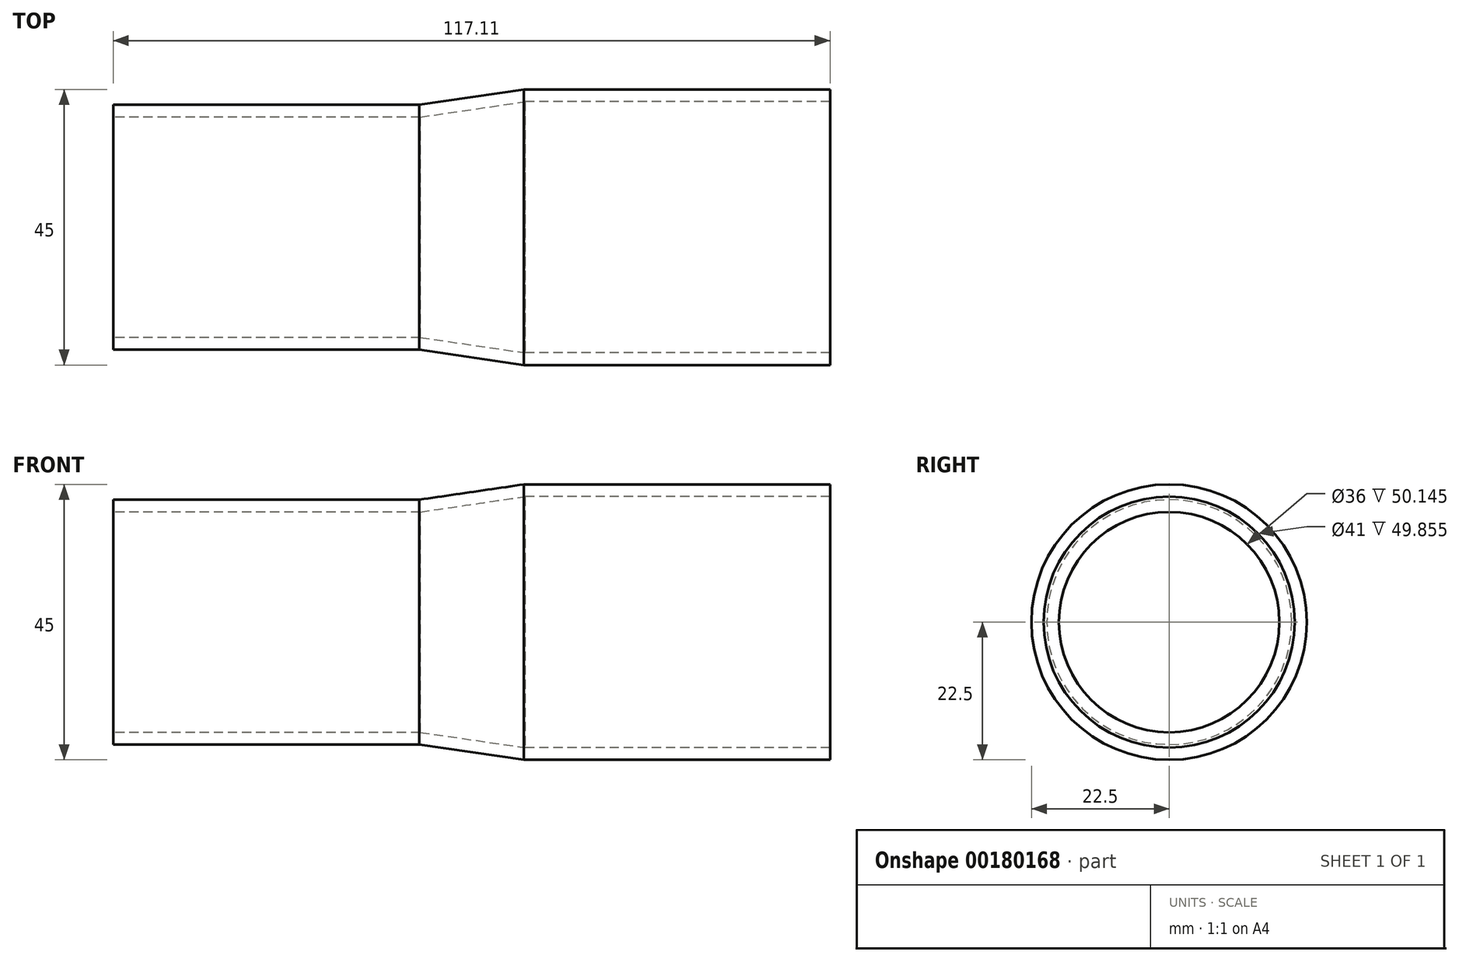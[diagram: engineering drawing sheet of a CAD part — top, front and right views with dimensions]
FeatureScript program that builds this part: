
annotation { "Feature Type Name" : "Feature", "Feature Type Description" : "" }
export const myFeature = defineFeature(function(context is Context, id is Id, definition is map)
    precondition{}
    {
        {
            var Q0;
            Q0=qCreatedBy(makeId("Front.planeOp"),FACE);
            var sketch = newSketch(context, id + "F0", { "sketchPlane" : qUnion([Q0])});
            skLineSegment(sketch, "E0", {"start": v(-49.34, 22.58) * mm, "end": v(0.66, 22.58) * mm});
            skLineSegment(sketch, "E1", {"start": v(0.66, 22.58) * mm, "end": v(17.77, 25.08) * mm});
            skLineSegment(sketch, "E2", {"start": v(17.77, 25.08) * mm, "end": v(67.77, 25.08) * mm});
            skLineSegment(sketch, "E3", {"start": v(-57.76, 2.58) * mm, "end": v(73.83, 2.58) * mm});
            skLineSegment(sketch, "E4.0", {"start": v(17.91, 23.08) * mm, "end": v(67.77, 23.08) * mm});
            skLineSegment(sketch, "E4.1", {"start": v(0.8, 20.58) * mm, "end": v(17.91, 23.08) * mm});
            skLineSegment(sketch, "E4.2", {"start": v(-49.34, 20.58) * mm, "end": v(0.8, 20.58) * mm});
            skLineSegment(sketch, "E5", {"start": v(67.77, 23.08) * mm, "end": v(67.77, 25.08) * mm});
            skLineSegment(sketch, "E6", {"start": v(-49.34, 22.58) * mm, "end": v(-49.34, 20.58) * mm});
            skSolve(sketch);
        }
        {
            var Q0;
            Q0=makeQuery(id+"F0.imprint","IMPRINT",FACE,{"disambiguationData":[TD([[makeQuery(id+"F0.imprint","IMPRINT",EDGE,{"derivedFrom":sQuery(id+"F0.wireOp",EDGE,"E0")}),-1.0]])]});
            var Q1;
            Q1=sQuery(id+"F0.wireOp",EDGE,"E3");
            revolve(context, id + "F1", {"entities" : qUnion([Q0]), "axis" : qUnion([Q1]), "revolveType" : RevolveType.FULL});
        }
    });
